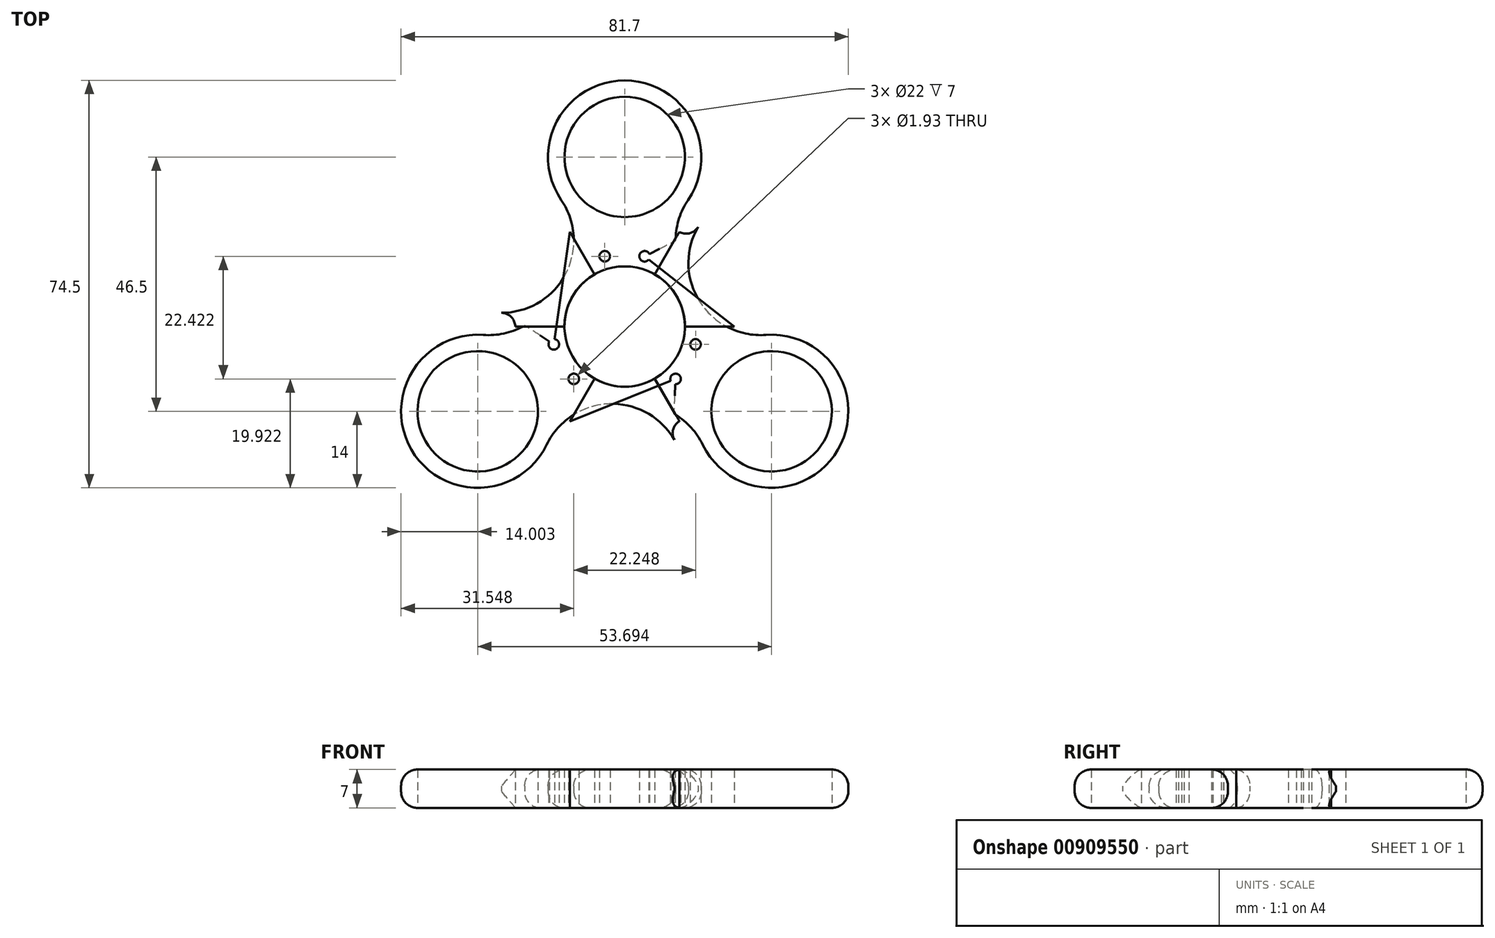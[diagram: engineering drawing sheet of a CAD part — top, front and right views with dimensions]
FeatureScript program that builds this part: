
annotation { "Feature Type Name" : "Feature", "Feature Type Description" : "" }
export const myFeature = defineFeature(function(context is Context, id is Id, definition is map)
    precondition{}
    {
        {
            var Q0;
            Q0=qCreatedBy(makeId("Top.planeOp"),FACE);
            var sketch = newSketch(context, id + "F0", { "sketchPlane" : qUnion([Q0])});
            skCircle(sketch, "E0", {"center": v(0, 0) * mm, "radius": 11 * mm});
            skLineSegment(sketch, "E1", {"start": v(0, 0) * mm, "end": v(22.5, 0) * mm});
            skLineSegment(sketch, "E2", {"start": v(22.5, 0) * mm, "end": v(22.5, 45) * mm});
            skLineSegment(sketch, "E3", {"start": v(22.5, 45) * mm, "end": v(-22.5, 45) * mm});
            skLineSegment(sketch, "E4", {"start": v(-22.5, 45) * mm, "end": v(-22.5, 0) * mm});
            skLineSegment(sketch, "E5", {"start": v(-22.5, 0) * mm, "end": v(0, 0) * mm});
            skCircle(sketch, "E6", {"center": v(0, 31) * mm, "radius": 11 * mm});
            skLineSegment(sketch, "E7", {"start": v(0, 45) * mm, "end": v(0, 42) * mm});
            skCircle(sketch, "E8", {"center": v(0, 31) * mm, "radius": 14 * mm});
            skLineSegment(sketch, "E9.bottom", {"start": v(-22.5, 0) * mm, "end": v(22.5, 0) * mm});
            skLineSegment(sketch, "E9.top", {"start": v(-22.5, 15.7) * mm, "end": v(22.5, 15.7) * mm});
            skLineSegment(sketch, "E9.left", {"start": v(-22.5, 0) * mm, "end": v(-22.5, 15.7) * mm});
            skLineSegment(sketch, "E9.right", {"start": v(22.5, 0) * mm, "end": v(22.5, 15.7) * mm});
            skCircle(sketch, "E10", {"center": v(-22.5, 15.7) * mm, "radius": 13.2 * mm});
            skCircle(sketch, "E11", {"center": v(22.5, 15.7) * mm, "radius": 13.2 * mm});
            skCircle(sketch, "E12", {"center": v(22.5, 0) * mm, "radius": 2.5 * mm});
            skCircle(sketch, "E13", {"center": v(-22.5, 0) * mm, "radius": 2.5 * mm});
            skLineSegment(sketch, "E14", {"start": v(-9.3, 15.7) * mm, "end": v(0, 11) * mm});
            skLineSegment(sketch, "E15", {"start": v(0, 11) * mm, "end": v(9.3, 15.7) * mm});
            skLineSegment(sketch, "E16", {"start": v(0, 11) * mm, "end": v(0, 15.7) * mm});
            skLineSegment(sketch, "E17", {"start": v(-20, 0) * mm, "end": v(0, 15.7) * mm});
            skLineSegment(sketch, "E18", {"start": v(20, 0) * mm, "end": v(0, 15.7) * mm});
            skCircle(sketch, "E19", {"center": v(-3.64, 12.84) * mm, "radius": 0.96 * mm});
            skCircle(sketch, "E20", {"center": v(3.64, 12.84) * mm, "radius": 0.96 * mm});
            skSolve(sketch);
        }
        {
            var Q0;
            Q0=makeQuery(id+"F0.imprint","IMPRINT",FACE,{"disambiguationData":[TD([[makeQuery(id+"F0.imprint","IMPRINT",EDGE,{"derivedFrom":sQuery(id+"F0.wireOp",EDGE,"E6")}),-1.0]])]});
            var Q1;
            {var subQ4=sQuery(id+"F0.wireOp",EDGE,"E8");var subQ6=sQuery(id+"F0.wireOp",EDGE,"E10");var subQ8=makeQuery(id+"F0.imprint","INTERSECT",VERTEX,{"derivedFrom":[subQ4,subQ6]});Q1=makeQuery(id+"F0.imprint","IMPRINT",FACE,{"disambiguationData":[TD([[makeQuery(id+"F0.imprint","IMPRINT",EDGE,{"disambiguationData":[TD([[subQ8,-1.0]])],"derivedFrom":subQ4}),-1.0]])]});}
            var Q2;
            {var subQ0=sQuery(id+"F0.wireOp",EDGE,"E15");var subQ5=sQuery(id+"F0.wireOp",EDGE,"E20");var subQ6=makeQuery(id+"F0.imprint","INTERSECT",VERTEX,{"disambiguationData":[OD(1.0)],"derivedFrom":[subQ0,subQ5]});Q2=makeQuery(id+"F0.imprint","IMPRINT",FACE,{"disambiguationData":[TD([[makeQuery(id+"F0.imprint","IMPRINT",EDGE,{"disambiguationData":[TD([[subQ6,-1.0]])],"derivedFrom":subQ5}),-1.0]])]});}
            var Q3;
            {var subQ3=sQuery(id+"F0.wireOp",EDGE,"E20");var subQ5=sQuery(id+"F0.wireOp",EDGE,"E15");var subQ6=makeQuery(id+"F0.imprint","INTERSECT",VERTEX,{"disambiguationData":[OD(1.0)],"derivedFrom":[subQ5,subQ3]});Q3=makeQuery(id+"F0.imprint","IMPRINT",FACE,{"disambiguationData":[TD([[makeQuery(id+"F0.imprint","IMPRINT",EDGE,{"disambiguationData":[TD([[subQ6,1.0]])],"derivedFrom":subQ3}),-1.0]])]});}
            var Q4;
            {var subQ0=sQuery(id+"F0.wireOp",EDGE,"E15");var subQ3=sQuery(id+"F0.wireOp",EDGE,"E20");var subQ4=makeQuery(id+"F0.imprint","INTERSECT",VERTEX,{"disambiguationData":[OD(0.0)],"derivedFrom":[subQ0,subQ3]});Q4=makeQuery(id+"F0.imprint","IMPRINT",FACE,{"disambiguationData":[TD([[makeQuery(id+"F0.imprint","IMPRINT",EDGE,{"disambiguationData":[TD([[subQ4,-1.0]])],"derivedFrom":subQ3}),-1.0]])]});}
            var Q5;
            {var subQ3=sQuery(id+"F0.wireOp",EDGE,"E19");var subQ7=sQuery(id+"F0.wireOp",EDGE,"E14");var subQ9=makeQuery(id+"F0.imprint","INTERSECT",VERTEX,{"disambiguationData":[OD(1.0)],"derivedFrom":[subQ7,subQ3]});Q5=makeQuery(id+"F0.imprint","IMPRINT",FACE,{"disambiguationData":[TD([[makeQuery(id+"F0.imprint","IMPRINT",EDGE,{"disambiguationData":[TD([[subQ9,1.0]])],"derivedFrom":subQ3}),-1.0]])]});}
            var Q6;
            {var subQ3=sQuery(id+"F0.wireOp",EDGE,"E19");var subQ7=sQuery(id+"F0.wireOp",EDGE,"E14");var subQ9=makeQuery(id+"F0.imprint","INTERSECT",VERTEX,{"disambiguationData":[OD(0.0)],"derivedFrom":[subQ7,subQ3]});Q6=makeQuery(id+"F0.imprint","IMPRINT",FACE,{"disambiguationData":[TD([[makeQuery(id+"F0.imprint","IMPRINT",EDGE,{"disambiguationData":[TD([[subQ9,-1.0]])],"derivedFrom":subQ3}),-1.0]])]});}
            var Q7;
            {var subQ0=sQuery(id+"F0.wireOp",EDGE,"E14");var subQ5=sQuery(id+"F0.wireOp",EDGE,"E19");var subQ6=makeQuery(id+"F0.imprint","INTERSECT",VERTEX,{"disambiguationData":[OD(0.0)],"derivedFrom":[subQ0,subQ5]});Q7=makeQuery(id+"F0.imprint","IMPRINT",FACE,{"disambiguationData":[TD([[makeQuery(id+"F0.imprint","IMPRINT",EDGE,{"disambiguationData":[TD([[subQ6,1.0]])],"derivedFrom":subQ5}),-1.0]])]});}
            var Q8;
            {var subQ0=sQuery(id+"F0.wireOp",EDGE,"E16");Q8=makeQuery(id+"F0.imprint","IMPRINT",FACE,{"disambiguationData":[TD([[makeQuery(id+"F0.imprint","IMPRINT",EDGE,{"derivedFrom":subQ0}),-1.0]])]});}
            var Q9;
            {var subQ0=sQuery(id+"F0.wireOp",EDGE,"E16");Q9=makeQuery(id+"F0.imprint","IMPRINT",FACE,{"disambiguationData":[TD([[makeQuery(id+"F0.imprint","IMPRINT",EDGE,{"derivedFrom":subQ0}),1.0]])]});}
            extrude(context, id + "F1", {"entities" : qUnion([Q0, Q1, Q2, Q3, Q4, Q5, Q6, Q7, Q8, Q9]), "depth" : 7 * mm, "offsetDistance" : 25 * mm});
        }
        {
            var Q0;
            Q0=qCreatedBy(makeId("Front.planeOp"),FACE);
            var sketch = newSketch(context, id + "F2", { "sketchPlane" : qUnion([Q0])});
            skLineSegment(sketch, "E21", {"start": v(0, 0) * mm, "end": v(0, 18.9) * mm});
            skSolve(sketch);
        }
        {
            var Q0;
            Q0=makeQuery(id+"F1.opExtrude","SWEPT_BODY",BODY,{"disambiguationData":[OSD([sQuery(id+"F0.wireOp",EDGE,"E0"),sQuery(id+"F0.wireOp",EDGE,"E6"),sQuery(id+"F0.wireOp",EDGE,"E8"),sQuery(id+"F0.wireOp",EDGE,"E9.bottom"),sQuery(id+"F0.wireOp",EDGE,"E10"),sQuery(id+"F0.wireOp",EDGE,"E11"),sQuery(id+"F0.wireOp",EDGE,"E12"),sQuery(id+"F0.wireOp",EDGE,"E13")])]});
            var Q1;
            Q1=sQuery(id+"F2.wireOp",EDGE,"E21");
            transform(context, id + "F3", {"entities" : qUnion([Q0]), "transformType" : TransformType.ROTATION, "transformAxis" : qUnion([Q1]), "angle" : 120 * degree, "makeCopy" : true});
        }
        {
            var Q0;
            Q0=makeQuery(id+"F1.opExtrude","SWEPT_BODY",BODY,{"disambiguationData":[OSD([sQuery(id+"F0.wireOp",EDGE,"E0"),sQuery(id+"F0.wireOp",EDGE,"E6"),sQuery(id+"F0.wireOp",EDGE,"E8"),sQuery(id+"F0.wireOp",EDGE,"E9.bottom"),sQuery(id+"F0.wireOp",EDGE,"E10"),sQuery(id+"F0.wireOp",EDGE,"E11"),sQuery(id+"F0.wireOp",EDGE,"E12"),sQuery(id+"F0.wireOp",EDGE,"E13")])]});
            var Q1;
            Q1=sQuery(id+"F2.wireOp",EDGE,"E21");
            transform(context, id + "F4", {"entities" : qUnion([Q0]), "transformType" : TransformType.ROTATION, "transformAxis" : qUnion([Q1]), "angle" : 240 * degree, "makeCopy" : true});
        }
        {
            var Q0;
            Q0=makeQuery(id+"F3.opPattern","COPY",EDGE,{"derivedFrom":makeQuery(id+"F1.opExtrude","CAP_EDGE",EDGE,{"disambiguationData":[OSD([sQuery(id+"F0.wireOp",EDGE,"E8")])],"isStart":false}),"instanceName":"1"});
            var Q1;
            Q1=makeQuery(id+"F3.opPattern","COPY",EDGE,{"derivedFrom":makeQuery(id+"F1.opExtrude","CAP_EDGE",EDGE,{"disambiguationData":[OSD([sQuery(id+"F0.wireOp",EDGE,"E8")])],"isStart":true}),"instanceName":"1"});
            var Q2;
            Q2=makeQuery(id+"F4.opPattern","COPY",EDGE,{"derivedFrom":makeQuery(id+"F1.opExtrude","CAP_EDGE",EDGE,{"disambiguationData":[OSD([sQuery(id+"F0.wireOp",EDGE,"E8")])],"isStart":false}),"instanceName":"1"});
            var Q3;
            Q3=makeQuery(id+"F4.opPattern","COPY",EDGE,{"derivedFrom":makeQuery(id+"F1.opExtrude","CAP_EDGE",EDGE,{"disambiguationData":[OSD([sQuery(id+"F0.wireOp",EDGE,"E8")])],"isStart":true}),"instanceName":"1"});
            var Q4;
            Q4=makeQuery(id+"F1.opExtrude","CAP_EDGE",EDGE,{"disambiguationData":[OSD([sQuery(id+"F0.wireOp",EDGE,"E8")])],"isStart":false});
            var Q5;
            Q5=makeQuery(id+"F1.opExtrude","CAP_EDGE",EDGE,{"disambiguationData":[OSD([sQuery(id+"F0.wireOp",EDGE,"E8")])],"isStart":true});
            fillet(context, id + "F5", {"entities" : qUnion([Q0, Q1, Q2, Q3, Q4, Q5]), "radius" : 3 * mm, "tangentPropagation" : true, "allowEdgeOverflow" : false});
        }
    });
